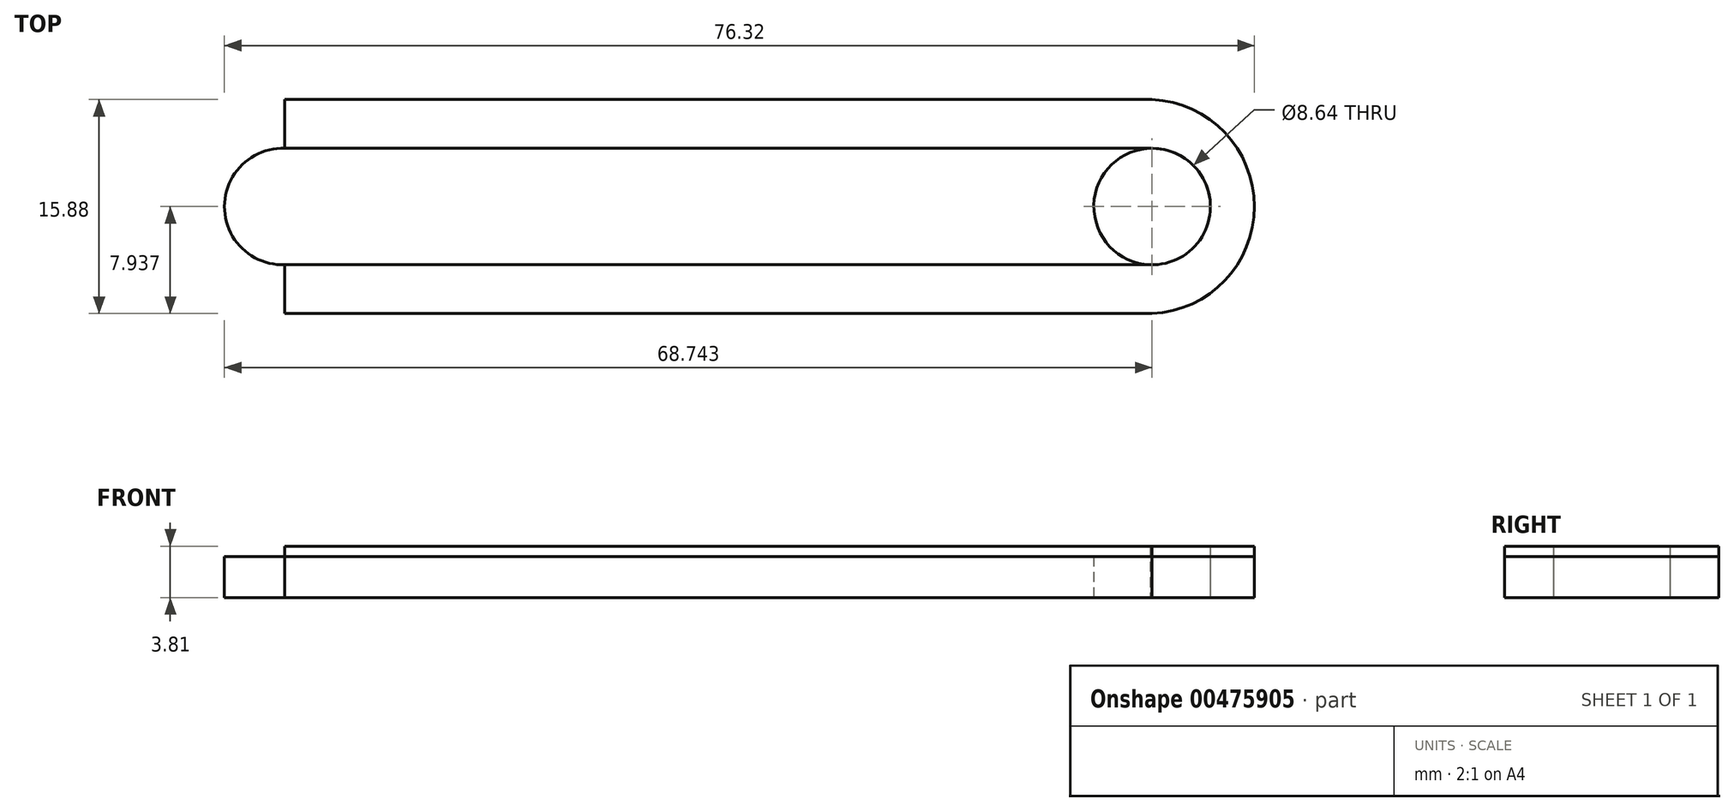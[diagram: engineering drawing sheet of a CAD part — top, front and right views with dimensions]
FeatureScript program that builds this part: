
annotation { "Feature Type Name" : "Feature", "Feature Type Description" : "" }
export const myFeature = defineFeature(function(context is Context, id is Id, definition is map)
    precondition{}
    {
        {
            var Q0;
            Q0=qCreatedBy(makeId("Top.planeOp"),FACE);
            var sketch = newSketch(context, id + "F0", { "sketchPlane" : qUnion([Q0])});
            skLineSegment(sketch, "E0.bottom", {"start": v(-26.02, 10.02) * mm, "end": v(38.24, 10.02) * mm});
            skLineSegment(sketch, "E0.top", {"start": v(-26.02, -5.86) * mm, "end": v(38.24, -5.86) * mm});
            skLineSegment(sketch, "E0.left", {"start": v(-26.02, 10.02) * mm, "end": v(-26.02, -5.86) * mm});
            skLineSegment(sketch, "E0.right", {"start": v(38.24, 10.02) * mm, "end": v(38.24, -5.86) * mm});
            skCircle(sketch, "E1", {"center": v(-26.18, 2.08) * mm, "radius": 7.94 * mm});
            skPoint(sketch, "E1.third.point", {"position": v(-33.84, 0) * mm});
            skCircle(sketch, "E2", {"center": v(37.87, 2.08) * mm, "radius": 7.95 * mm});
            skPoint(sketch, "E2.third.point", {"position": v(45.82, 2.08) * mm});
            skPoint(sketch, "E2.third.point.positionSnap0", {"position": v(38.24, 2.08) * mm});
            skCircle(sketch, "E3", {"center": v(38.24, 2.08) * mm, "radius": 4.32 * mm});
            skCircle(sketch, "E4", {"center": v(-26.18, 2.08) * mm, "radius": 4.32 * mm});
            skLineSegment(sketch, "E5.bottom", {"start": v(-26.02, -2.24) * mm, "end": v(38.24, -2.24) * mm});
            skLineSegment(sketch, "E5.top", {"start": v(-26.02, 6.4) * mm, "end": v(38.24, 6.4) * mm});
            skLineSegment(sketch, "E5.left", {"start": v(-26.02, -2.24) * mm, "end": v(-26.02, 6.4) * mm});
            skLineSegment(sketch, "E5.right", {"start": v(38.24, -2.24) * mm, "end": v(38.24, 6.4) * mm});
            skSolve(sketch);
        }
        {
            var Q0;
            {var subQ1=sQuery(id+"F0.wireOp",EDGE,"E0.top");var subQ3=sQuery(id+"F0.wireOp",EDGE,"E2");var subQ4=makeQuery(id+"F0.imprint","INTERSECT",VERTEX,{"derivedFrom":[subQ1,subQ3]});Q0=makeQuery(id+"F0.imprint","IMPRINT",FACE,{"disambiguationData":[TD([[makeQuery(id+"F0.imprint","IMPRINT",EDGE,{"disambiguationData":[TD([[subQ4,1.0]])],"derivedFrom":subQ3}),-1.0]])]});}
            var Q1;
            {var subQ1=sQuery(id+"F0.wireOp",EDGE,"E0.bottom");var subQ3=sQuery(id+"F0.wireOp",EDGE,"E2");var subQ4=makeQuery(id+"F0.imprint","INTERSECT",VERTEX,{"derivedFrom":[subQ1,subQ3]});Q1=makeQuery(id+"F0.imprint","IMPRINT",FACE,{"disambiguationData":[TD([[makeQuery(id+"F0.imprint","IMPRINT",EDGE,{"disambiguationData":[TD([[subQ4,-1.0]])],"derivedFrom":subQ3}),-1.0]])]});}
            var Q2;
            {var subQ0=sQuery(id+"F0.wireOp",EDGE,"E5.left");var subQ1=sQuery(id+"F0.wireOp",EDGE,"E4");var subQ4=makeQuery(id+"F0.imprint","INTERSECT",VERTEX,{"derivedFrom":[subQ1,subQ0]});Q2=makeQuery(id+"F0.imprint","IMPRINT",FACE,{"disambiguationData":[TD([[makeQuery(id+"F0.imprint","IMPRINT",EDGE,{"disambiguationData":[TD([[subQ4,-1.0]])],"derivedFrom":subQ0}),1.0]])]});}
            var Q3;
            {var subQ0=sQuery(id+"F0.wireOp",EDGE,"E1");var subQ3=sQuery(id+"F0.wireOp",EDGE,"E5.top");var subQ5=makeQuery(id+"F0.imprint","INTERSECT",VERTEX,{"derivedFrom":[subQ0,subQ3]});Q3=makeQuery(id+"F0.imprint","IMPRINT",FACE,{"disambiguationData":[TD([[makeQuery(id+"F0.imprint","IMPRINT",EDGE,{"disambiguationData":[TD([[subQ5,-1.0]])],"derivedFrom":subQ0}),1.0]])]});}
            var Q4;
            {var subQ0=sQuery(id+"F0.wireOp",EDGE,"E1");var subQ3=sQuery(id+"F0.wireOp",EDGE,"E5.bottom");var subQ5=makeQuery(id+"F0.imprint","INTERSECT",VERTEX,{"derivedFrom":[subQ0,subQ3]});Q4=makeQuery(id+"F0.imprint","IMPRINT",FACE,{"disambiguationData":[TD([[makeQuery(id+"F0.imprint","IMPRINT",EDGE,{"disambiguationData":[TD([[subQ5,1.0]])],"derivedFrom":subQ0}),1.0]])]});}
            var Q5;
            {var subQ5=sQuery(id+"F0.wireOp",EDGE,"E2");var subQ6=sQuery(id+"F0.wireOp",EDGE,"E0.top");var subQ7=makeQuery(id+"F0.imprint","INTERSECT",VERTEX,{"derivedFrom":[subQ6,subQ5]});Q5=makeQuery(id+"F0.imprint","IMPRINT",FACE,{"disambiguationData":[TD([[makeQuery(id+"F0.imprint","IMPRINT",EDGE,{"disambiguationData":[TD([[subQ7,1.0]])],"derivedFrom":subQ5}),1.0]])]});}
            var Q6;
            {var subQ1=sQuery(id+"F0.wireOp",EDGE,"E0.right");var subQ3=sQuery(id+"F0.wireOp",EDGE,"E3");var subQ5=makeQuery(id+"F0.imprint","INTERSECT",VERTEX,{"derivedFrom":[subQ1,subQ3]});Q6=makeQuery(id+"F0.imprint","IMPRINT",FACE,{"disambiguationData":[TD([[makeQuery(id+"F0.imprint","IMPRINT",EDGE,{"disambiguationData":[TD([[subQ5,-1.0]])],"derivedFrom":subQ1}),1.0]])]});}
            var Q7;
            {var subQ0=sQuery(id+"F0.wireOp",EDGE,"E2");var subQ2=sQuery(id+"F0.wireOp",EDGE,"E0.bottom");var subQ4=makeQuery(id+"F0.imprint","INTERSECT",VERTEX,{"derivedFrom":[subQ2,subQ0]});Q7=makeQuery(id+"F0.imprint","IMPRINT",FACE,{"disambiguationData":[TD([[makeQuery(id+"F0.imprint","IMPRINT",EDGE,{"disambiguationData":[TD([[subQ4,-1.0]])],"derivedFrom":subQ0}),1.0]])]});}
            extrude(context, id + "F1", {"entities" : qUnion([Q0, Q1, Q2, Q3, Q4, Q5, Q6, Q7]), "depth" : 3.8 * mm});
        }
        {
            var Q0;
            {var subQ1=sQuery(id+"F0.wireOp",EDGE,"E0.bottom");var subQ3=sQuery(id+"F0.wireOp",EDGE,"E2");var subQ4=makeQuery(id+"F0.imprint","INTERSECT",VERTEX,{"derivedFrom":[subQ1,subQ3]});Q0=makeQuery(id+"F0.imprint","IMPRINT",FACE,{"disambiguationData":[TD([[makeQuery(id+"F0.imprint","IMPRINT",EDGE,{"disambiguationData":[TD([[subQ4,-1.0]])],"derivedFrom":subQ3}),-1.0]])]});}
            var Q1;
            {var subQ0=sQuery(id+"F0.wireOp",EDGE,"E5.top");var subQ1=sQuery(id+"F0.wireOp",EDGE,"E1");var subQ2=makeQuery(id+"F0.imprint","INTERSECT",VERTEX,{"derivedFrom":[subQ1,subQ0]});Q1=makeQuery(id+"F0.imprint","IMPRINT",FACE,{"disambiguationData":[TD([[makeQuery(id+"F0.imprint","IMPRINT",EDGE,{"disambiguationData":[TD([[subQ2,1.0]])],"derivedFrom":subQ1}),-1.0]])]});}
            var Q2;
            {var subQ0=sQuery(id+"F0.wireOp",EDGE,"E2");var subQ2=sQuery(id+"F0.wireOp",EDGE,"E0.bottom");var subQ4=makeQuery(id+"F0.imprint","INTERSECT",VERTEX,{"derivedFrom":[subQ2,subQ0]});Q2=makeQuery(id+"F0.imprint","IMPRINT",FACE,{"disambiguationData":[TD([[makeQuery(id+"F0.imprint","IMPRINT",EDGE,{"disambiguationData":[TD([[subQ4,-1.0]])],"derivedFrom":subQ0}),1.0]])]});}
            var Q3;
            {var subQ0=sQuery(id+"F0.wireOp",EDGE,"E5.top");var subQ1=sQuery(id+"F0.wireOp",EDGE,"E2");var subQ2=makeQuery(id+"F0.imprint","INTERSECT",VERTEX,{"derivedFrom":[subQ1,subQ0]});Q3=makeQuery(id+"F0.imprint","IMPRINT",FACE,{"disambiguationData":[TD([[makeQuery(id+"F0.imprint","IMPRINT",EDGE,{"disambiguationData":[TD([[subQ2,-1.0]])],"derivedFrom":subQ1}),1.0]])]});}
            var Q4;
            {var subQ0=sQuery(id+"F0.wireOp",EDGE,"E5.right");Q4=makeQuery(id+"F0.imprint","IMPRINT",FACE,{"disambiguationData":[TD([[makeQuery(id+"F0.imprint","IMPRINT",EDGE,{"derivedFrom":subQ0}),1.0]])]});}
            var Q5;
            {var subQ0=sQuery(id+"F0.wireOp",EDGE,"E5.right");Q5=makeQuery(id+"F0.imprint","IMPRINT",FACE,{"disambiguationData":[TD([[makeQuery(id+"F0.imprint","IMPRINT",EDGE,{"derivedFrom":subQ0}),-1.0]])]});}
            var Q6;
            {var subQ1=sQuery(id+"F0.wireOp",EDGE,"E0.right");var subQ3=sQuery(id+"F0.wireOp",EDGE,"E3");var subQ5=makeQuery(id+"F0.imprint","INTERSECT",VERTEX,{"derivedFrom":[subQ1,subQ3]});Q6=makeQuery(id+"F0.imprint","IMPRINT",FACE,{"disambiguationData":[TD([[makeQuery(id+"F0.imprint","IMPRINT",EDGE,{"disambiguationData":[TD([[subQ5,-1.0]])],"derivedFrom":subQ1}),1.0]])]});}
            var Q7;
            {var subQ5=sQuery(id+"F0.wireOp",EDGE,"E2");var subQ6=sQuery(id+"F0.wireOp",EDGE,"E0.top");var subQ7=makeQuery(id+"F0.imprint","INTERSECT",VERTEX,{"derivedFrom":[subQ6,subQ5]});Q7=makeQuery(id+"F0.imprint","IMPRINT",FACE,{"disambiguationData":[TD([[makeQuery(id+"F0.imprint","IMPRINT",EDGE,{"disambiguationData":[TD([[subQ7,1.0]])],"derivedFrom":subQ5}),1.0]])]});}
            var Q8;
            {var subQ1=sQuery(id+"F0.wireOp",EDGE,"E0.top");var subQ3=sQuery(id+"F0.wireOp",EDGE,"E2");var subQ4=makeQuery(id+"F0.imprint","INTERSECT",VERTEX,{"derivedFrom":[subQ1,subQ3]});Q8=makeQuery(id+"F0.imprint","IMPRINT",FACE,{"disambiguationData":[TD([[makeQuery(id+"F0.imprint","IMPRINT",EDGE,{"disambiguationData":[TD([[subQ4,1.0]])],"derivedFrom":subQ3}),-1.0]])]});}
            var Q9;
            {var subQ0=sQuery(id+"F0.wireOp",EDGE,"E5.left");var subQ1=sQuery(id+"F0.wireOp",EDGE,"E4");var subQ4=makeQuery(id+"F0.imprint","INTERSECT",VERTEX,{"derivedFrom":[subQ1,subQ0]});Q9=makeQuery(id+"F0.imprint","IMPRINT",FACE,{"disambiguationData":[TD([[makeQuery(id+"F0.imprint","IMPRINT",EDGE,{"disambiguationData":[TD([[subQ4,-1.0]])],"derivedFrom":subQ0}),1.0]])]});}
            var Q10;
            {var subQ0=sQuery(id+"F0.wireOp",EDGE,"E5.left");var subQ1=sQuery(id+"F0.wireOp",EDGE,"E4");var subQ3=makeQuery(id+"F0.imprint","INTERSECT",VERTEX,{"derivedFrom":[subQ1,subQ0]});Q10=makeQuery(id+"F0.imprint","IMPRINT",FACE,{"disambiguationData":[TD([[makeQuery(id+"F0.imprint","IMPRINT",EDGE,{"disambiguationData":[TD([[subQ3,-1.0]])],"derivedFrom":subQ1}),1.0]])]});}
            var Q11;
            {var subQ0=sQuery(id+"F0.wireOp",EDGE,"E5.left");var subQ1=sQuery(id+"F0.wireOp",EDGE,"E4");var subQ3=makeQuery(id+"F0.imprint","INTERSECT",VERTEX,{"derivedFrom":[subQ1,subQ0]});Q11=makeQuery(id+"F0.imprint","IMPRINT",FACE,{"disambiguationData":[TD([[makeQuery(id+"F0.imprint","IMPRINT",EDGE,{"disambiguationData":[TD([[subQ3,1.0]])],"derivedFrom":subQ1}),1.0]])]});}
            var Q12;
            {var subQ0=sQuery(id+"F0.wireOp",EDGE,"E1");var subQ3=sQuery(id+"F0.wireOp",EDGE,"E5.top");var subQ5=makeQuery(id+"F0.imprint","INTERSECT",VERTEX,{"derivedFrom":[subQ0,subQ3]});Q12=makeQuery(id+"F0.imprint","IMPRINT",FACE,{"disambiguationData":[TD([[makeQuery(id+"F0.imprint","IMPRINT",EDGE,{"disambiguationData":[TD([[subQ5,-1.0]])],"derivedFrom":subQ0}),1.0]])]});}
            var Q13;
            {var subQ5=sQuery(id+"F0.wireOp",EDGE,"E1");var subQ7=sQuery(id+"F0.wireOp",EDGE,"E5.top");var subQ9=makeQuery(id+"F0.imprint","INTERSECT",VERTEX,{"derivedFrom":[subQ5,subQ7]});Q13=makeQuery(id+"F0.imprint","IMPRINT",FACE,{"disambiguationData":[TD([[makeQuery(id+"F0.imprint","IMPRINT",EDGE,{"disambiguationData":[TD([[subQ9,1.0]])],"derivedFrom":subQ5}),1.0]])]});}
            var Q14;
            {var subQ0=sQuery(id+"F0.wireOp",EDGE,"E1");var subQ3=sQuery(id+"F0.wireOp",EDGE,"E5.bottom");var subQ5=makeQuery(id+"F0.imprint","INTERSECT",VERTEX,{"derivedFrom":[subQ0,subQ3]});Q14=makeQuery(id+"F0.imprint","IMPRINT",FACE,{"disambiguationData":[TD([[makeQuery(id+"F0.imprint","IMPRINT",EDGE,{"disambiguationData":[TD([[subQ5,1.0]])],"derivedFrom":subQ0}),1.0]])]});}
            extrude(context, id + "F2", {"entities" : qUnion([Q0, Q1, Q2, Q3, Q4, Q5, Q6, Q7, Q8, Q9, Q10, Q11, Q12, Q13, Q14]), "depth" : 3.05 * mm});
        }
    });
